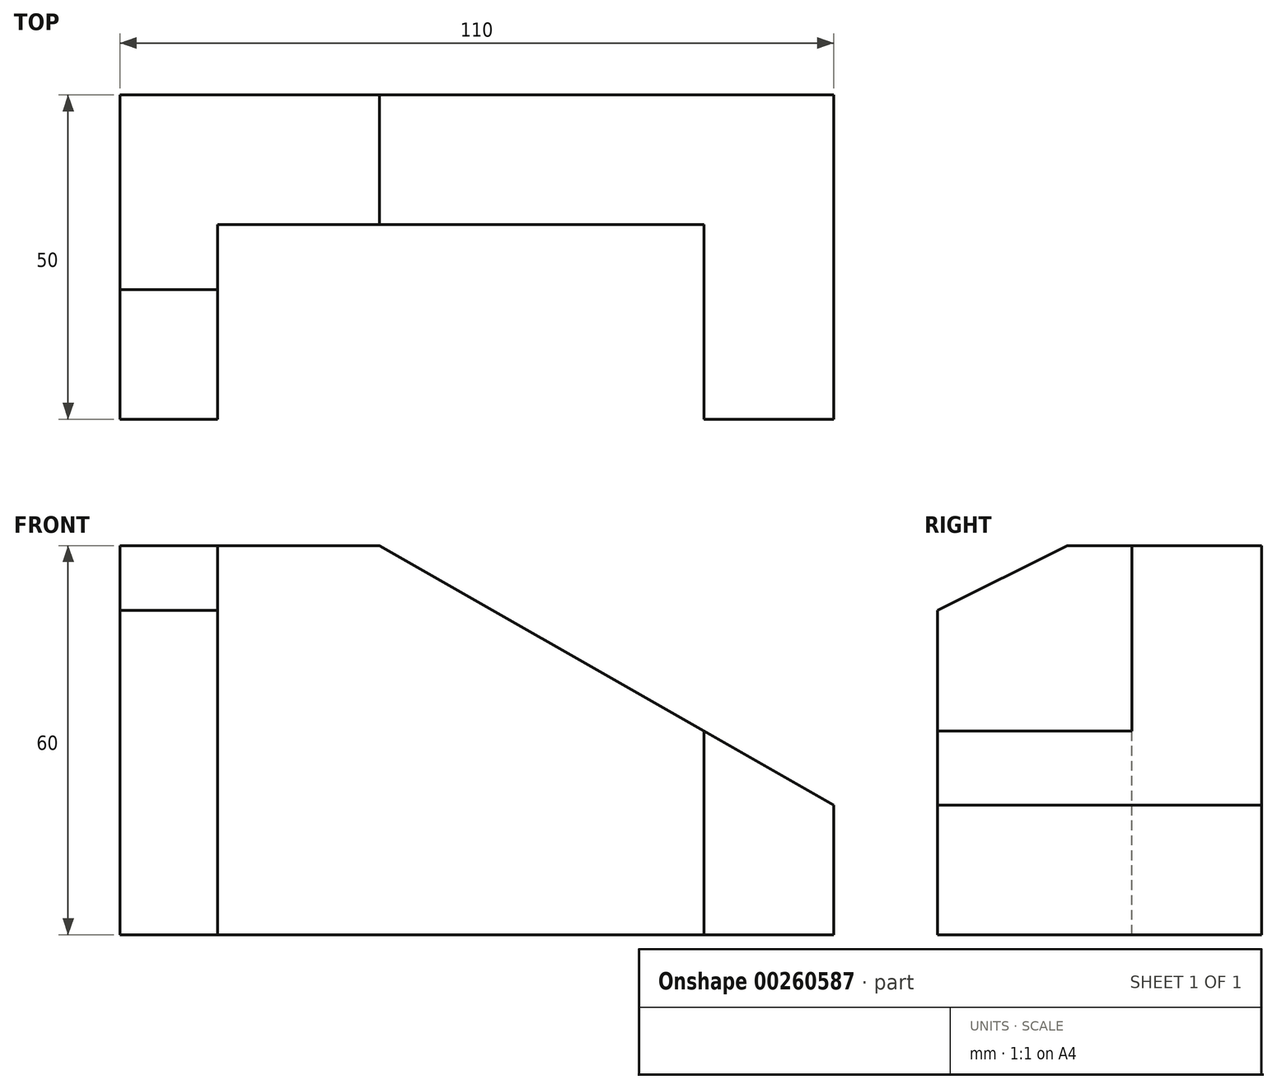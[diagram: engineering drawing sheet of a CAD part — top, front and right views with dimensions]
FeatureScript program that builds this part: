
annotation { "Feature Type Name" : "Feature", "Feature Type Description" : "" }
export const myFeature = defineFeature(function(context is Context, id is Id, definition is map)
    precondition{}
    {
        {
            assignVariable(context, id + "F0", {"name" : "B", "anyValue" : 60});
        }
        {
            var Q0;
            Q0=qCreatedBy(makeId("Top.planeOp"),FACE);
            var sketch = newSketch(context, id + "F1", { "sketchPlane" : qUnion([Q0])});
            skLineSegment(sketch, "E0.bottom", {"start": v(55, -25) * mm, "end": v(-55, -25) * mm});
            skLineSegment(sketch, "E0.top", {"start": v(55, 25) * mm, "end": v(-55, 25) * mm});
            skLineSegment(sketch, "E0.left", {"start": v(55, -25) * mm, "end": v(55, 25) * mm});
            skLineSegment(sketch, "E0.right", {"start": v(-55, -25) * mm, "end": v(-55, 25) * mm});
            skPoint(sketch, "E0.middle", {"position": v(0, 0) * mm});
            skSolve(sketch);
        }
        {
            var Q0;
            Q0 = qSketchRegion(id + "F1", true);
            extrude(context, id + "F2", {"entities" : qUnion([Q0]), "depth" : (getVariable(context, 'B')) * mm});
        }
        {
            var Q0;
            Q0=makeQuery(id+"F2.opExtrude","CAP_FACE",FACE,{"disambiguationData":[OSD([sQuery(id+"F1.wireOp",EDGE,"E0.bottom"),sQuery(id+"F1.wireOp",EDGE,"E0.top"),sQuery(id+"F1.wireOp",EDGE,"E0.left"),sQuery(id+"F1.wireOp",EDGE,"E0.right")])],"isStart":false});
            var sketch = newSketch(context, id + "F3", { "sketchPlane" : qUnion([Q0])});
            skLineSegment(sketch, "E1.bottom", {"start": v(0, -25) * mm, "end": v(35, -25) * mm});
            skLineSegment(sketch, "E1.top", {"start": v(0, 5) * mm, "end": v(35, 5) * mm});
            skLineSegment(sketch, "E1.left", {"start": v(0, -25) * mm, "end": v(0, 5) * mm});
            skLineSegment(sketch, "E1.right", {"start": v(35, -25) * mm, "end": v(35, 5) * mm});
            skLineSegment(sketch, "E2.bottom", {"start": v(0, -25) * mm, "end": v(-40, -25) * mm});
            skLineSegment(sketch, "E2.top", {"start": v(0, 5) * mm, "end": v(-40, 5) * mm});
            skLineSegment(sketch, "E2.right", {"start": v(-40, -25) * mm, "end": v(-40, 5) * mm});
            skSolve(sketch);
        }
        {
            var Q0;
            Q0=makeQuery(id+"F3.imprint","IMPRINT",FACE,{"disambiguationData":[TD([[makeQuery(id+"F3.imprint","IMPRINT",EDGE,{"derivedFrom":sQuery(id+"F3.wireOp",EDGE,"E2.bottom")}),-1.0]])]});
            var Q1;
            Q1=makeQuery(id+"F3.imprint","IMPRINT",FACE,{"disambiguationData":[TD([[makeQuery(id+"F3.imprint","IMPRINT",EDGE,{"derivedFrom":sQuery(id+"F3.wireOp",EDGE,"E1.bottom")}),-1.0]])]});
            extrude(context, id + "F4", {"entities" : qUnion([Q0, Q1]), "operationType" : NewBodyOperationType.REMOVE, "endBound" : BoundingType.THROUGH_ALL, "oppositeDirection" : true, "depth" : 25 * mm});
        }
        {
            var Q0;
            Q0=makeQuery(id+"F2.opExtrude","SWEPT_FACE",FACE,{"disambiguationData":[OSD([sQuery(id+"F1.wireOp",EDGE,"E0.right")])]});
            var sketch = newSketch(context, id + "F5", { "sketchPlane" : qUnion([Q0])});
            skLineSegment(sketch, "E3", {"start": v(25, 60) * mm, "end": v(25, 50) * mm});
            skLineSegment(sketch, "E4", {"start": v(25, 50) * mm, "end": v(5, 60) * mm});
            skLineSegment(sketch, "E5", {"start": v(5, 60) * mm, "end": v(25, 60) * mm});
            skSolve(sketch);
        }
        {
            var Q0;
            Q0=makeQuery(id+"F5.imprint","IMPRINT",FACE,{"disambiguationData":[TD([[makeQuery(id+"F5.imprint","IMPRINT",EDGE,{"derivedFrom":sQuery(id+"F5.wireOp",EDGE,"E3")}),-1.0]])]});
            extrude(context, id + "F6", {"entities" : qUnion([Q0]), "operationType" : NewBodyOperationType.REMOVE, "endBound" : BoundingType.UP_TO_NEXT, "oppositeDirection" : true, "depth" : 25 * mm});
        }
        {
            var Q0;
            Q0=makeQuery(id+"F2.opExtrude","SWEPT_FACE",FACE,{"disambiguationData":[OSD([sQuery(id+"F1.wireOp",EDGE,"E0.top")])]});
            var sketch = newSketch(context, id + "F7", { "sketchPlane" : qUnion([Q0])});
            skLineSegment(sketch, "E6", {"start": v(-55, 60) * mm, "end": v(-55, 20) * mm});
            skLineSegment(sketch, "E7", {"start": v(-55, 20) * mm, "end": v(15, 60) * mm});
            skLineSegment(sketch, "E8", {"start": v(15, 60) * mm, "end": v(-55, 60) * mm});
            skSolve(sketch);
        }
        {
            var Q0;
            Q0=makeQuery(id+"F7.imprint","IMPRINT",FACE,{"disambiguationData":[TD([[makeQuery(id+"F7.imprint","IMPRINT",EDGE,{"derivedFrom":sQuery(id+"F7.wireOp",EDGE,"E6")}),1.0]])]});
            extrude(context, id + "F8", {"entities" : qUnion([Q0]), "operationType" : NewBodyOperationType.REMOVE, "endBound" : BoundingType.THROUGH_ALL, "oppositeDirection" : true, "depth" : 25 * mm});
        }
    });
